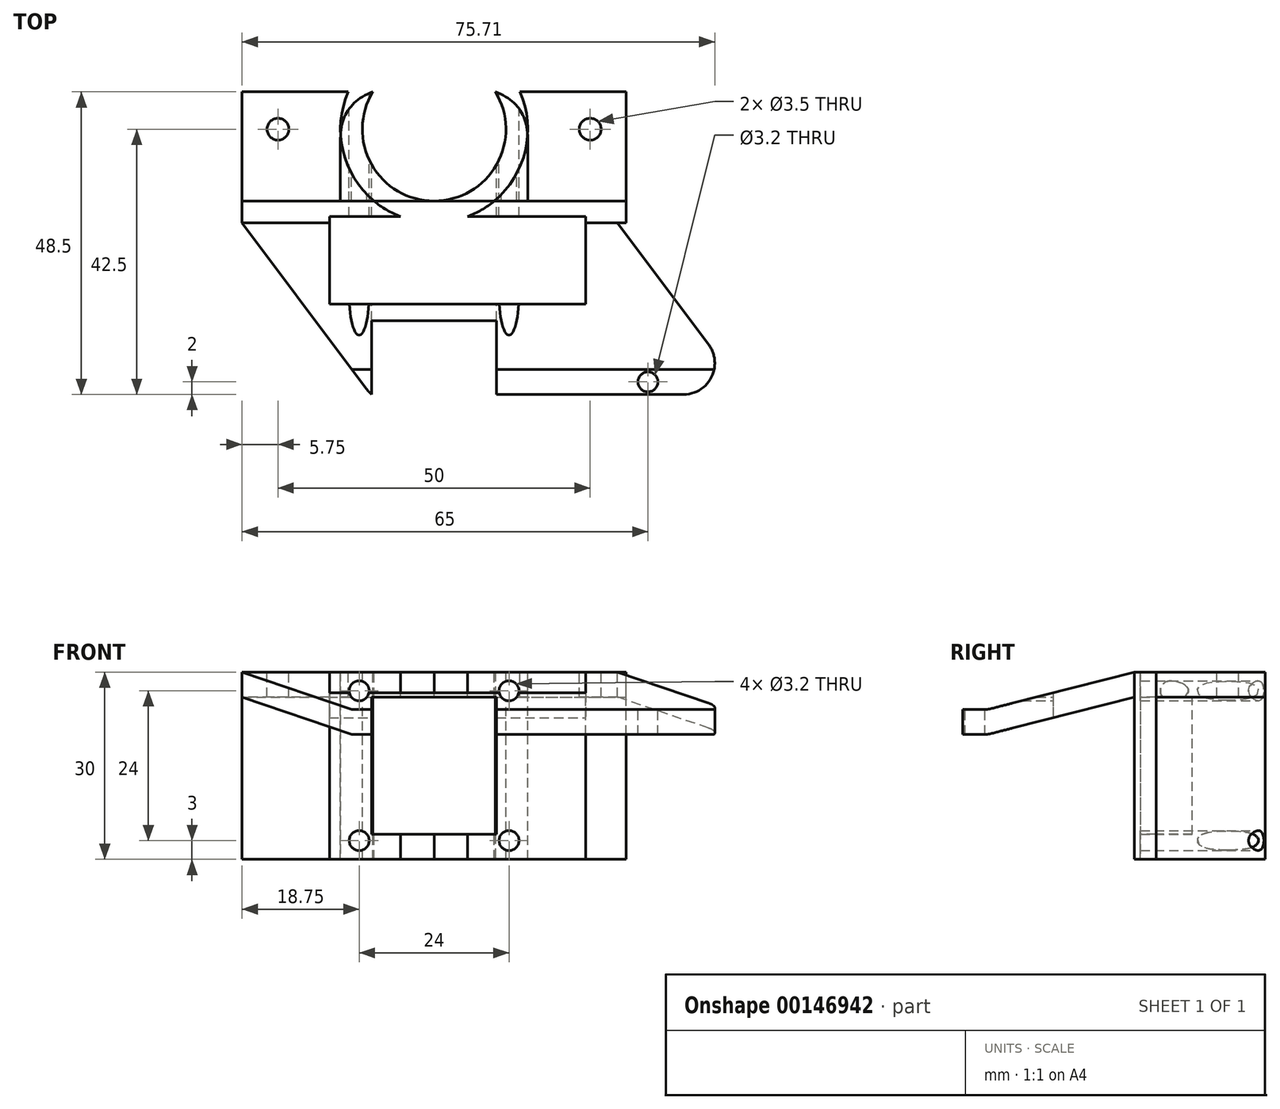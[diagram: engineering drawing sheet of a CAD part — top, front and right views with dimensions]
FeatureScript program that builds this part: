
annotation { "Feature Type Name" : "Feature", "Feature Type Description" : "" }
export const myFeature = defineFeature(function(context is Context, id is Id, definition is map)
    precondition{}
    {
        {
            var Q0;
            Q0=qCreatedBy(makeId("Top.planeOp"),FACE);
            var sketch = newSketch(context, id + "F0", { "sketchPlane" : qUnion([Q0])});
            skLineSegment(sketch, "E0", {"start": v(-25, 0) * mm, "end": v(25, 0) * mm, "construction": true});
            skCircle(sketch, "E1", {"center": v(0, 0) * mm, "radius": 15 * mm, "construction": true});
            skCircle(sketch, "E2", {"center": v(-25, 0) * mm, "radius": 1.75 * mm});
            skCircle(sketch, "E3", {"center": v(25, 0) * mm, "radius": 1.75 * mm});
            skLineSegment(sketch, "E4", {"start": v(-26.75, 0) * mm, "end": v(-30.75, 0) * mm, "construction": true});
            skLineSegment(sketch, "E5", {"start": v(26.75, 0) * mm, "end": v(30.75, 0) * mm, "construction": true});
            skLineSegment(sketch, "E6.bottom", {"start": v(-30.75, 6) * mm, "end": v(30.75, 6) * mm});
            skLineSegment(sketch, "E6.top", {"start": v(-30.75, -15) * mm, "end": v(30.75, -15) * mm});
            skLineSegment(sketch, "E6.left", {"start": v(-30.75, 6) * mm, "end": v(-30.75, -15) * mm});
            skLineSegment(sketch, "E6.right", {"start": v(30.75, 6) * mm, "end": v(30.75, -15) * mm});
            skArc(sketch, "E7", {"start": v(13.75, 6) * mm, "mid": v(0, -15) * mm, "end": v(-13.75, 6) * mm});
            skLineSegment(sketch, "E8.top", {"start": v(-30.75, -11.5) * mm, "end": v(30.75, -11.5) * mm});
            skLineSegment(sketch, "E8.left", {"start": v(-30.75, -15) * mm, "end": v(-30.75, -11.5) * mm});
            skLineSegment(sketch, "E8.right", {"start": v(30.75, -15) * mm, "end": v(30.75, -11.5) * mm});
            skCircle(sketch, "E9", {"center": v(0, 0) * mm, "radius": 11.5 * mm});
            skLineSegment(sketch, "E10", {"start": v(15, -11.5) * mm, "end": v(15, 0) * mm});
            skLineSegment(sketch, "E11", {"start": v(-15, 0) * mm, "end": v(-15, -11.5) * mm});
            skSolve(sketch);
        }
        {
            var Q0;
            Q0=makeQuery(id+"F0.imprint","IMPRINT",FACE,{"disambiguationData":[TD([[makeQuery(id+"F0.imprint","IMPRINT",EDGE,{"derivedFrom":sQuery(id+"F0.wireOp",EDGE,"E2")}),-1.0]])]});
            var Q1;
            {var subQ0=sQuery(id+"F0.wireOp",EDGE,"E11");Q1=makeQuery(id+"F0.imprint","IMPRINT",FACE,{"disambiguationData":[TD([[makeQuery(id+"F0.imprint","IMPRINT",EDGE,{"derivedFrom":subQ0}),1.0]])]});}
            var Q2;
            {var subQ0=sQuery(id+"F0.wireOp",EDGE,"E10");Q2=makeQuery(id+"F0.imprint","IMPRINT",FACE,{"disambiguationData":[TD([[makeQuery(id+"F0.imprint","IMPRINT",EDGE,{"derivedFrom":subQ0}),1.0]])]});}
            var Q3;
            Q3=makeQuery(id+"F0.imprint","IMPRINT",FACE,{"disambiguationData":[TD([[makeQuery(id+"F0.imprint","IMPRINT",EDGE,{"derivedFrom":sQuery(id+"F0.wireOp",EDGE,"E3")}),-1.0]])]});
            extrude(context, id + "F1", {"entities" : qUnion([Q0, Q1, Q2, Q3]), "oppositeDirection" : true, "depth" : 4 * mm});
        }
        {
            var Q0;
            Q0=makeQuery(id+"F0.imprint","IMPRINT",FACE,{"disambiguationData":[TD([[makeQuery(id+"F0.imprint","IMPRINT",EDGE,{"derivedFrom":sQuery(id+"F0.wireOp",EDGE,"E6.top")}),1.0]])]});
            var Q1;
            {var subQ0=sQuery(id+"F0.wireOp",EDGE,"E7");var subQ3=sQuery(id+"F0.wireOp",EDGE,"E6.bottom");var subQ4=makeQuery(id+"F0.imprint","INTERSECT",VERTEX,{"disambiguationData":[OD(1.0)],"derivedFrom":[subQ3,subQ0]});Q1=makeQuery(id+"F0.imprint","IMPRINT",FACE,{"disambiguationData":[TD([[makeQuery(id+"F0.imprint","IMPRINT",EDGE,{"disambiguationData":[TD([[subQ4,-1.0]])],"derivedFrom":subQ3}),-1.0]])]});}
            var Q2;
            {var subQ0=sQuery(id+"F0.wireOp",EDGE,"E11");Q2=makeQuery(id+"F0.imprint","IMPRINT",FACE,{"disambiguationData":[TD([[makeQuery(id+"F0.imprint","IMPRINT",EDGE,{"derivedFrom":subQ0}),1.0]])]});}
            var Q3;
            {var subQ0=sQuery(id+"F0.wireOp",EDGE,"E10");Q3=makeQuery(id+"F0.imprint","IMPRINT",FACE,{"disambiguationData":[TD([[makeQuery(id+"F0.imprint","IMPRINT",EDGE,{"derivedFrom":subQ0}),1.0]])]});}
            var Q4;
            {var subQ0=sQuery(id+"F0.wireOp",EDGE,"E7");var subQ4=sQuery(id+"F0.wireOp",EDGE,"E6.bottom");var subQ5=makeQuery(id+"F0.imprint","INTERSECT",VERTEX,{"disambiguationData":[OD(0.0)],"derivedFrom":[subQ4,subQ0]});Q4=makeQuery(id+"F0.imprint","IMPRINT",FACE,{"disambiguationData":[TD([[makeQuery(id+"F0.imprint","IMPRINT",EDGE,{"disambiguationData":[TD([[subQ5,1.0]])],"derivedFrom":subQ4}),-1.0]])]});}
            var Q5;
            {var subQ0=sQuery(id+"F0.wireOp",EDGE,"E7");var subQ1=makeQuery(id+"F0.imprint","INTERSECT",VERTEX,{"derivedFrom":[subQ0,sQuery(id+"F0.wireOp",EDGE,"E6.top")]});Q5=makeQuery(id+"F0.imprint","IMPRINT",FACE,{"disambiguationData":[TD([[makeQuery(id+"F0.imprint","IMPRINT",EDGE,{"disambiguationData":[TD([[subQ1,1.0]])],"derivedFrom":subQ0}),-1.0]])]});}
            extrude(context, id + "F2", {"entities" : qUnion([Q0, Q1, Q2, Q3, Q4, Q5]), "oppositeDirection" : true, "depth" : 30 * mm});
        }
        {
            var Q0;
            {var subQ0=sQuery(id+"F0.wireOp",EDGE,"E7");var subQ1=sQuery(id+"F0.wireOp",EDGE,"E6.bottom");Q0=makeQuery(id+"F2.opExtrude","SWEPT_EDGE",EDGE,{"disambiguationData":[OSD([subQ1,subQ0]),TDD([makeQuery(id+"F0.imprint","INTERSECT",VERTEX,{"disambiguationData":[OD(1.0)],"derivedFrom":[subQ1,subQ0]})])]});}
            var Q1;
            {var subQ0=sQuery(id+"F0.wireOp",EDGE,"E7");var subQ1=sQuery(id+"F0.wireOp",EDGE,"E6.bottom");Q1=makeQuery(id+"F2.opExtrude","SWEPT_EDGE",EDGE,{"disambiguationData":[OSD([subQ1,subQ0]),TDD([makeQuery(id+"F0.imprint","INTERSECT",VERTEX,{"disambiguationData":[OD(0.0)],"derivedFrom":[subQ1,subQ0]})])]});}
            fillet(context, id + "F3", {"entities" : qUnion([Q0, Q1]), "radius" : 8 * mm, "tangentPropagation" : true, "rho" : 0.5, "crossSection" : FilletCrossSection.CONIC, "allowEdgeOverflow" : false});
        }
        {
            var Q0;
            Q0=qCreatedBy(makeId("Front.planeOp"),FACE);
            var sketch = newSketch(context, id + "F4", { "sketchPlane" : qUnion([Q0])});
            skLineSegment(sketch, "E12", {"start": v(0, 0) * mm, "end": v(0, -30) * mm, "construction": true});
            skLineSegment(sketch, "E13.bottom", {"start": v(10, -4) * mm, "end": v(-10, -4) * mm});
            skLineSegment(sketch, "E13.top", {"start": v(10, -26) * mm, "end": v(-10, -26) * mm});
            skLineSegment(sketch, "E13.left", {"start": v(10, -4) * mm, "end": v(10, -26) * mm});
            skLineSegment(sketch, "E13.right", {"start": v(-10, -4) * mm, "end": v(-10, -26) * mm});
            skPoint(sketch, "E13.middle", {"position": v(0, -15) * mm});
            skLineSegment(sketch, "E14.bottom", {"start": v(12, -3) * mm, "end": v(-12, -3) * mm, "construction": true});
            skLineSegment(sketch, "E14.top", {"start": v(12, -27) * mm, "end": v(-12, -27) * mm, "construction": true});
            skLineSegment(sketch, "E14.left", {"start": v(12, -3) * mm, "end": v(12, -27) * mm, "construction": true});
            skLineSegment(sketch, "E14.right", {"start": v(-12, -3) * mm, "end": v(-12, -27) * mm, "construction": true});
            skCircle(sketch, "E15", {"center": v(12, -3) * mm, "radius": 1.6 * mm});
            skCircle(sketch, "E16", {"center": v(-12, -3) * mm, "radius": 1.6 * mm});
            skCircle(sketch, "E17", {"center": v(-12, -27) * mm, "radius": 1.6 * mm});
            skCircle(sketch, "E18", {"center": v(12, -27) * mm, "radius": 1.6 * mm});
            skSolve(sketch);
        }
        {
            var Q0;
            Q0=qCreatedBy(makeId("Right.planeOp"),FACE);
            var sketch = newSketch(context, id + "F5", { "sketchPlane" : qUnion([Q0])});
            skLineSegment(sketch, "E19", {"start": v(-40.5, 0) * mm, "end": v(0, 0) * mm, "construction": true});
            skLineSegment(sketch, "E20", {"start": v(-40.5, 0) * mm, "end": v(-40.5, -10) * mm, "construction": true});
            skLineSegment(sketch, "E21", {"start": v(-42.5, -10) * mm, "end": v(-38.5, -10) * mm});
            skLineSegment(sketch, "E22", {"start": v(-42.5, -10) * mm, "end": v(-42.5, -6) * mm});
            skLineSegment(sketch, "E23", {"start": v(-42.5, -6) * mm, "end": v(-38.5, -6) * mm});
            skLineSegment(sketch, "E24", {"start": v(-38.5, -6) * mm, "end": v(-38.5, -10) * mm});
            skLineSegment(sketch, "E25", {"start": v(-38.5, -6) * mm, "end": v(-15, 0) * mm});
            skLineSegment(sketch, "E26", {"start": v(-15, 0) * mm, "end": v(-15, -4) * mm});
            skLineSegment(sketch, "E27", {"start": v(-15, -4) * mm, "end": v(-15, 0) * mm});
            skLineSegment(sketch, "E28", {"start": v(-38.5, -10) * mm, "end": v(-15, -4) * mm});
            skSolve(sketch);
        }
        {
            var Q0;
            Q0=makeQuery(id+"F5.imprint","IMPRINT",FACE,{"disambiguationData":[TD([[makeQuery(id+"F5.imprint","IMPRINT",EDGE,{"derivedFrom":sQuery(id+"F5.wireOp",EDGE,"E21")}),1.0]])]});
            var Q1;
            Q1=makeQuery(id+"F5.imprint","IMPRINT",FACE,{"disambiguationData":[TD([[makeQuery(id+"F5.imprint","IMPRINT",EDGE,{"derivedFrom":sQuery(id+"F5.wireOp",EDGE,"E24")}),1.0]])]});
            extrude(context, id + "F6", {"entities" : qUnion([Q0, Q1]), "endBound" : BoundingType.SYMMETRIC, "depth" : 100 * mm});
        }
        {
            var Q0;
            Q0=makeQuery(id+"F4.imprint","IMPRINT",FACE,{"disambiguationData":[TD([[makeQuery(id+"F4.imprint","IMPRINT",EDGE,{"derivedFrom":sQuery(id+"F4.wireOp",EDGE,"E13.bottom")}),1.0]])]});
            extrude(context, id + "F7", {"entities" : qUnion([Q0]), "operationType" : NewBodyOperationType.REMOVE, "depth" : 111 * mm});
        }
        {
            var Q0;
            Q0=makeQuery(id+"F4.imprint","IMPRINT",FACE,{"disambiguationData":[TD([[makeQuery(id+"F4.imprint","IMPRINT",EDGE,{"derivedFrom":sQuery(id+"F4.wireOp",EDGE,"E15")}),1.0]])]});
            var Q1;
            Q1=makeQuery(id+"F4.imprint","IMPRINT",FACE,{"disambiguationData":[TD([[makeQuery(id+"F4.imprint","IMPRINT",EDGE,{"derivedFrom":sQuery(id+"F4.wireOp",EDGE,"E16")}),1.0]])]});
            var Q2;
            Q2=makeQuery(id+"F4.imprint","IMPRINT",FACE,{"disambiguationData":[TD([[makeQuery(id+"F4.imprint","IMPRINT",EDGE,{"derivedFrom":sQuery(id+"F4.wireOp",EDGE,"E17")}),1.0]])]});
            var Q3;
            Q3=makeQuery(id+"F4.imprint","IMPRINT",FACE,{"disambiguationData":[TD([[makeQuery(id+"F4.imprint","IMPRINT",EDGE,{"derivedFrom":sQuery(id+"F4.wireOp",EDGE,"E18")}),1.0]])]});
            extrude(context, id + "F8", {"entities" : qUnion([Q0, Q1, Q2, Q3]), "operationType" : NewBodyOperationType.REMOVE, "endBound" : BoundingType.SYMMETRIC, "depth" : 100 * mm});
        }
        {
            var Q0;
            Q0=qCreatedBy(makeId("Top.planeOp"),FACE);
            var sketch = newSketch(context, id + "F9", { "sketchPlane" : qUnion([Q0])});
            skLineSegment(sketch, "E29", {"start": v(-30.75, -40.5) * mm, "end": v(-5.75, -40.5) * mm, "construction": true});
            skLineSegment(sketch, "E30", {"start": v(-5.75, -40.5) * mm, "end": v(34.25, -40.5) * mm, "construction": true});
            skLineSegment(sketch, "E31", {"start": v(-30.75, -15) * mm, "end": v(-30.75, -38.5) * mm, "construction": true});
            skCircle(sketch, "E32", {"center": v(-5.75, -40.5) * mm, "radius": 1.6 * mm});
            skCircle(sketch, "E33", {"center": v(34.25, -40.5) * mm, "radius": 1.6 * mm});
            skLineSegment(sketch, "E34", {"start": v(-30.75, -15) * mm, "end": v(-10.16, -42.52) * mm});
            skLineSegment(sketch, "E35", {"start": v(49.96, -42.52) * mm, "end": v(29.37, -15) * mm});
            skLineSegment(sketch, "E36", {"start": v(29.37, -15) * mm, "end": v(-30.75, -15) * mm});
            skLineSegment(sketch, "E37", {"start": v(-30.75, -15) * mm, "end": v(-55.36, -15) * mm});
            skLineSegment(sketch, "E38", {"start": v(-55.36, -15) * mm, "end": v(-55.36, -47.4) * mm});
            skLineSegment(sketch, "E39", {"start": v(-55.36, -47.4) * mm, "end": v(60.75, -47.4) * mm});
            skLineSegment(sketch, "E40", {"start": v(60.75, -47.4) * mm, "end": v(60.75, -15) * mm});
            skLineSegment(sketch, "E41", {"start": v(60.75, -15) * mm, "end": v(29.37, -15) * mm});
            skLineSegment(sketch, "E42", {"start": v(49.96, -42.52) * mm, "end": v(-10.16, -42.52) * mm});
            skSolve(sketch);
        }
        {
            var Q0;
            Q0=makeQuery(id+"F9.imprint","IMPRINT",FACE,{"disambiguationData":[TD([[makeQuery(id+"F9.imprint","IMPRINT",EDGE,{"derivedFrom":sQuery(id+"F9.wireOp",EDGE,"E32")}),1.0]])]});
            var Q1;
            Q1=makeQuery(id+"F9.imprint","IMPRINT",FACE,{"disambiguationData":[TD([[makeQuery(id+"F9.imprint","IMPRINT",EDGE,{"derivedFrom":sQuery(id+"F9.wireOp",EDGE,"E33")}),1.0]])]});
            var Q2;
            Q2=makeQuery(id+"F9.imprint","IMPRINT",FACE,{"disambiguationData":[TD([[makeQuery(id+"F9.imprint","IMPRINT",EDGE,{"derivedFrom":sQuery(id+"F9.wireOp",EDGE,"E34")}),-1.0]])]});
            extrude(context, id + "F10", {"entities" : qUnion([Q0, Q1, Q2]), "operationType" : NewBodyOperationType.REMOVE, "oppositeDirection" : true, "depth" : 60 * mm});
        }
        {
            var Q0;
            Q0=makeQuery(id+"F10.boolean.opBoolean","COPY",EDGE,{"derivedFrom":makeQuery(id+"F10.opExtrude","SWEPT_EDGE",EDGE,{"disambiguationData":[OSD([sQuery(id+"F9.wireOp",EDGE,"E34"),sQuery(id+"F9.wireOp",EDGE,"LZ9jtE0i-OAHh-45kW-sWNW-y6qPTdp6gWfT")])]})});
            var Q1;
            Q1=makeQuery(id+"F10.boolean.opBoolean","COPY",EDGE,{"derivedFrom":makeQuery(id+"F10.opExtrude","SWEPT_EDGE",EDGE,{"disambiguationData":[OSD([sQuery(id+"F9.wireOp",EDGE,"LZ9jtE0i-OAHh-45kW-sWNW-y6qPTdp6gWfT"),sQuery(id+"F9.wireOp",EDGE,"E35")])]})});
            var Q2;
            Q2=makeQuery(id+"F10.boolean.opBoolean","INTERSECT",EDGE,{"derivedFrom":[makeQuery(id+"F6.opExtrude","SWEPT_FACE",FACE,{"disambiguationData":[OSD([sQuery(id+"F5.wireOp",EDGE,"E22")])]}),makeQuery(id+"F10.opExtrude","SWEPT_FACE",FACE,{"disambiguationData":[OSD([sQuery(id+"F9.wireOp",EDGE,"E34")])]})]});
            var Q3;
            Q3=makeQuery(id+"F10.boolean.opBoolean","INTERSECT",EDGE,{"derivedFrom":[makeQuery(id+"F6.opExtrude","SWEPT_FACE",FACE,{"disambiguationData":[OSD([sQuery(id+"F5.wireOp",EDGE,"E22")])]}),makeQuery(id+"F10.opExtrude","SWEPT_FACE",FACE,{"disambiguationData":[OSD([sQuery(id+"F9.wireOp",EDGE,"E35")])]})]});
            fillet(context, id + "F11", {"entities" : qUnion([Q0, Q1, Q2, Q3]), "radius" : 5 * mm, "tangentPropagation" : true, "allowEdgeOverflow" : false});
        }
        {
            var Q0;
            Q0=qCreatedBy(makeId("Front.planeOp"),FACE);
            var sketch = newSketch(context, id + "F12", { "sketchPlane" : qUnion([Q0])});
            skLineSegment(sketch, "E43", {"start": v(-16.75, 0) * mm, "end": v(-16.75, -31) * mm});
            skLineSegment(sketch, "E44", {"start": v(-16.75, 0) * mm, "end": v(24.25, 0) * mm});
            skLineSegment(sketch, "E45", {"start": v(24.25, 0) * mm, "end": v(24.25, -31) * mm});
            skLineSegment(sketch, "E46", {"start": v(24.25, -31) * mm, "end": v(-16.75, -31) * mm});
            skLineSegment(sketch, "E47", {"start": v(-16.75, -31) * mm, "end": v(24.25, -31) * mm});
            skSolve(sketch);
        }
        {
            var Q0;
            Q0 = qSketchRegion(id + "F12", true);
            extrude(context, id + "F13", {"entities" : qUnion([Q0]), "operationType" : NewBodyOperationType.REMOVE, "depth" : 28 * mm, "hasSecondDirection" : true, "secondDirectionOppositeDirection" : false, "secondDirectionDepth" : 14 * mm});
        }
    });
